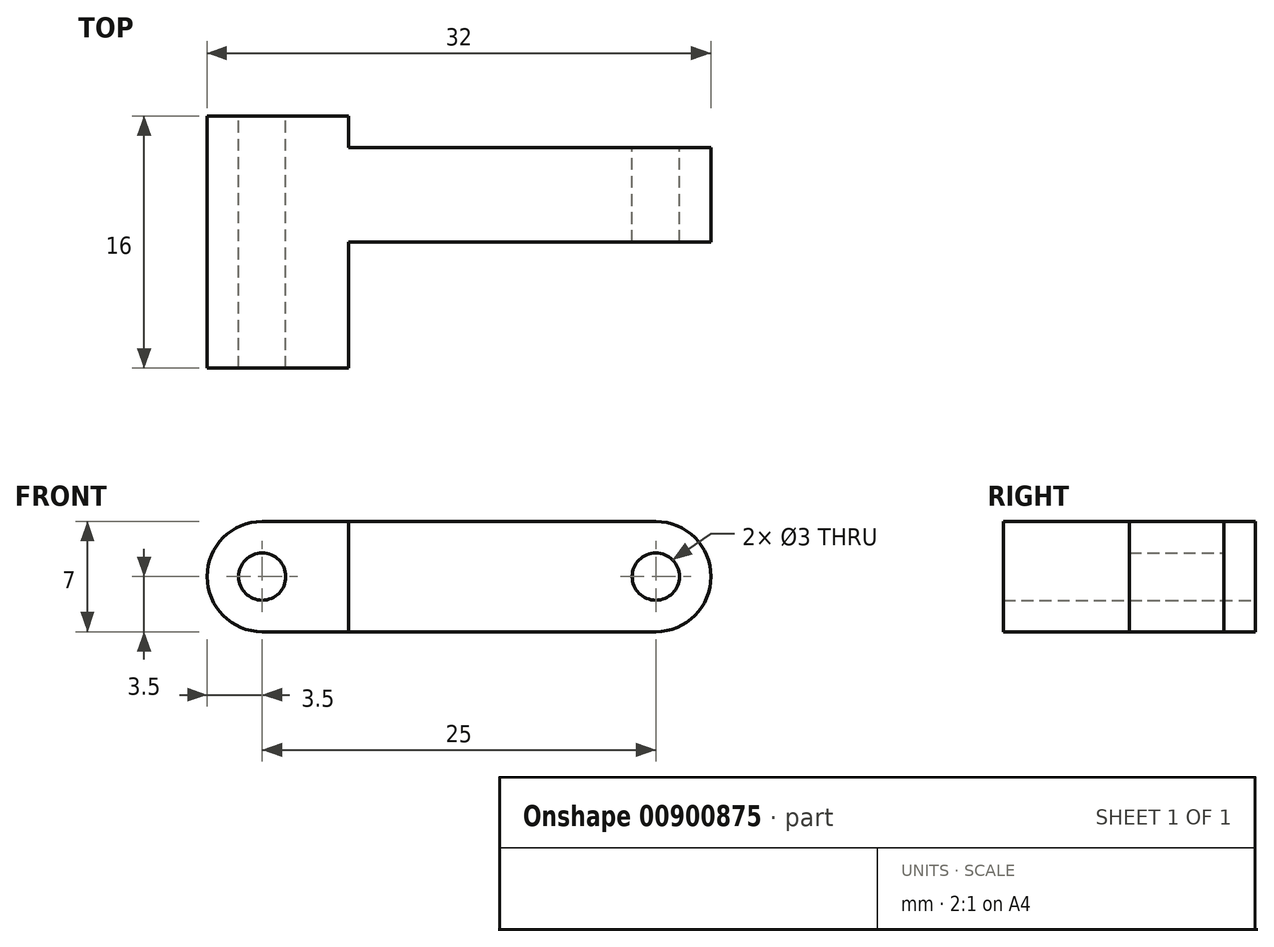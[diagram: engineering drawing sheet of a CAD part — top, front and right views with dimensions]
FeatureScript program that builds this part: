
annotation { "Feature Type Name" : "Feature", "Feature Type Description" : "" }
export const myFeature = defineFeature(function(context is Context, id is Id, definition is map)
    precondition{}
    {
        {
            var Q0;
            Q0=qCreatedBy(makeId("Front.planeOp"),FACE);
            var sketch = newSketch(context, id + "F0", { "sketchPlane" : qUnion([Q0])});
            skCircle(sketch, "E0", {"center": v(-12.5, 0) * mm, "radius": 1.5 * mm});
            skArc(sketch, "E1", {"start": v(-12.5, 3.5) * mm, "mid": v(-16, 0) * mm, "end": v(-12.5, -3.5) * mm});
            skCircle(sketch, "E2", {"center": v(12.5, 0) * mm, "radius": 1.5 * mm});
            skArc(sketch, "E3", {"start": v(12.5, -3.5) * mm, "mid": v(16, 0) * mm, "end": v(12.5, 3.5) * mm});
            skLineSegment(sketch, "E4", {"start": v(-12.5, 3.5) * mm, "end": v(12.5, 3.5) * mm});
            skLineSegment(sketch, "E5", {"start": v(-12.5, -3.5) * mm, "end": v(12.5, -3.5) * mm});
            skSolve(sketch);
        }
        {
            var Q0;
            Q0 = qSketchRegion(id + "F0", true);
            extrude(context, id + "F1", {"entities" : qUnion([Q0]), "endBound" : BoundingType.SYMMETRIC, "depth" : 16 * mm, "offsetDistance" : 25 * mm});
        }
        {
            var Q0;
            Q0=makeQuery(id+"F1.opExtrude","SWEPT_FACE",FACE,{"disambiguationData":[OSD([sQuery(id+"F0.wireOp",EDGE,"E4")])]});
            var sketch = newSketch(context, id + "F2", { "sketchPlane" : qUnion([Q0])});
            skLineSegment(sketch, "E6.bottom", {"start": v(-7, 6) * mm, "end": v(38.74, 6) * mm});
            skLineSegment(sketch, "E6.top", {"start": v(-7, 26.37) * mm, "end": v(38.74, 26.37) * mm});
            skLineSegment(sketch, "E6.left", {"start": v(-7, 6) * mm, "end": v(-7, 26.37) * mm});
            skLineSegment(sketch, "E6.right", {"start": v(38.74, 6) * mm, "end": v(38.74, 26.37) * mm});
            skLineSegment(sketch, "E7.bottom", {"start": v(-7, 0) * mm, "end": v(43.31, 0) * mm});
            skLineSegment(sketch, "E7.top", {"start": v(-7, -22.25) * mm, "end": v(43.31, -22.25) * mm});
            skLineSegment(sketch, "E7.left", {"start": v(-7, 0) * mm, "end": v(-7, -22.25) * mm});
            skLineSegment(sketch, "E7.right", {"start": v(43.31, 0) * mm, "end": v(43.31, -22.25) * mm});
            skSolve(sketch);
        }
        {
            var Q0;
            {var subQ2=sQuery(id+"F2.wireOp",EDGE,"E6.top");Q0=makeQuery(id+"F2.imprint","IMPRINT",FACE,{"disambiguationData":[TD([[makeQuery(id+"F2.imprint","IMPRINT",EDGE,{"derivedFrom":subQ2}),-1.0]])]});}
            var Q1;
            {var subQ2=sQuery(id+"F2.wireOp",EDGE,"E7.top");Q1=makeQuery(id+"F2.imprint","IMPRINT",FACE,{"disambiguationData":[TD([[makeQuery(id+"F2.imprint","IMPRINT",EDGE,{"derivedFrom":subQ2}),1.0]])]});}
            var Q2;
            {var subQ0=sQuery(id+"F2.wireOp",EDGE,"E7.left");var subQ1=sQuery(id+"F2.wireOp",EDGE,"E7.bottom");var subQ2=makeQuery(id+"F2.imprint","INTERSECT",VERTEX,{"derivedFrom":[subQ1,subQ0]});Q2=makeQuery(id+"F2.imprint","IMPRINT",FACE,{"disambiguationData":[TD([[makeQuery(id+"F2.imprint","IMPRINT",EDGE,{"disambiguationData":[TD([[subQ2,-1.0]])],"derivedFrom":subQ0}),1.0]])]});}
            var Q3;
            {var subQ0=sQuery(id+"F2.wireOp",EDGE,"E6.left");var subQ1=sQuery(id+"F2.wireOp",EDGE,"E6.bottom");var subQ2=makeQuery(id+"F2.imprint","INTERSECT",VERTEX,{"derivedFrom":[subQ1,subQ0]});Q3=makeQuery(id+"F2.imprint","IMPRINT",FACE,{"disambiguationData":[TD([[makeQuery(id+"F2.imprint","IMPRINT",EDGE,{"disambiguationData":[TD([[subQ2,-1.0]])],"derivedFrom":subQ0}),-1.0]])]});}
            extrude(context, id + "F3", {"entities" : qUnion([Q0, Q1, Q2, Q3]), "operationType" : NewBodyOperationType.REMOVE, "endBound" : BoundingType.THROUGH_ALL, "oppositeDirection" : true, "depth" : 25 * mm, "offsetDistance" : 25 * mm});
        }
    });
